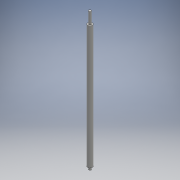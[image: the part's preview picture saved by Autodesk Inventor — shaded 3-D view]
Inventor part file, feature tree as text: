
AUTODESK INVENTOR PART (.ipt)
format: ipt  version: 2016 SP1 (Build 200210100, 210)  size: 95,232 bytes
history: native  units: mm
features: extrude x3, sketch x3
ambient origin geometry x8: Origin, YZ Plane, XZ Plane, XY Plane, X Axis, Y Axis, Z Axis, Center Point
bodies: Solid1 (feature_tree)
feature tree (6):
  extrude  "Extrusion1"  Depth=6.0mm TaperAngle=0.0deg
  extrude  "Extrusion2"  Depth=265.0mm TaperAngle=0.0deg
  extrude  "Extrusion3"  Depth=25.0mm TaperAngle=0.0deg
  sketch  "Sketch1"  dims[d0=5.0mm d1=6.0mm d2=0.0mm]
  sketch  "Sketch2"  dims[d3=10.0mm d4=265.0mm d5=0.0mm]
  sketch  "Sketch3"  dims[d6=5.0mm d7=25.0mm d8=0.0mm]
